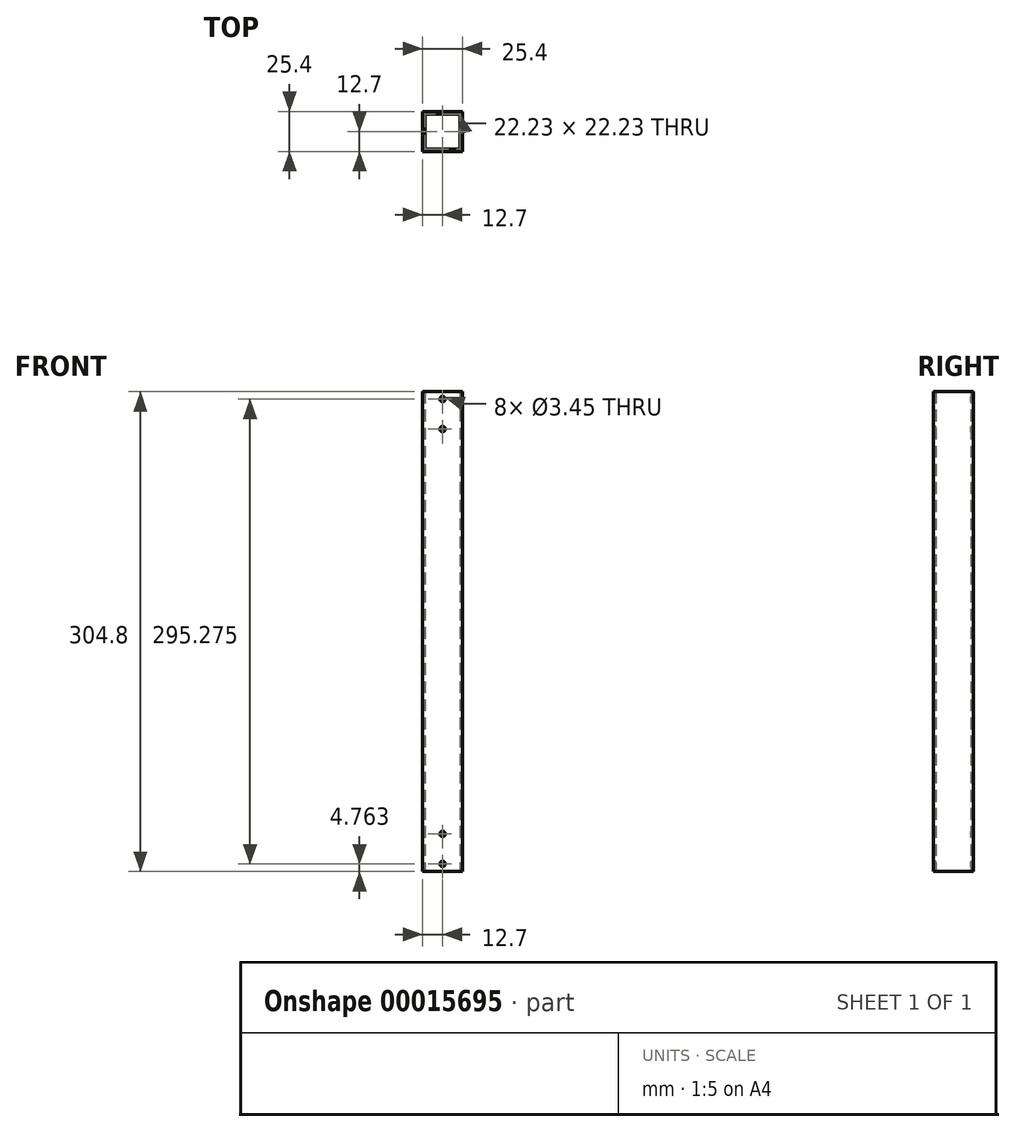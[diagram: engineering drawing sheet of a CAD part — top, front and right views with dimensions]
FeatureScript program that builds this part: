
annotation { "Feature Type Name" : "Feature", "Feature Type Description" : "" }
export const myFeature = defineFeature(function(context is Context, id is Id, definition is map)
    precondition{}
    {
        {
            var Q0;
            Q0=qCreatedBy(makeId("Top.planeOp"),FACE);
            var sketch = newSketch(context, id + "F0", { "sketchPlane" : qUnion([Q0])});
            skLineSegment(sketch, "E0.rect.bottom", {"start": v(12.7, -12.7) * mm, "end": v(-12.7, -12.7) * mm});
            skLineSegment(sketch, "E0.rect.top", {"start": v(12.7, 12.7) * mm, "end": v(-12.7, 12.7) * mm});
            skLineSegment(sketch, "E0.rect.left", {"start": v(12.7, -12.7) * mm, "end": v(12.7, 12.7) * mm});
            skLineSegment(sketch, "E0.rect.right", {"start": v(-12.7, -12.7) * mm, "end": v(-12.7, 12.7) * mm});
            skPoint(sketch, "E0.rect.middle", {"position": v(0, 0) * mm});
            skLineSegment(sketch, "E1.rect.bottom", {"start": v(11.11, -11.11) * mm, "end": v(-11.11, -11.11) * mm});
            skLineSegment(sketch, "E1.rect.top", {"start": v(11.11, 11.11) * mm, "end": v(-11.11, 11.11) * mm});
            skLineSegment(sketch, "E1.rect.left", {"start": v(11.11, -11.11) * mm, "end": v(11.11, 11.11) * mm});
            skLineSegment(sketch, "E1.rect.right", {"start": v(-11.11, -11.11) * mm, "end": v(-11.11, 11.11) * mm});
            skLineSegment(sketch, "E2", {"start": v(0, -11.11) * mm, "end": v(0, -12.7) * mm, "construction": true});
            skSolve(sketch);
        }
        {
            var Q0;
            Q0=qSketchRegion(id+"F0",true);
            extrude(context, id + "F1", {"entities" : qUnion([Q0]), "depth" : 304.8 * mm});
        }
        {
            var Q0;
            Q0=makeQuery(id+"F1.opExtrude","SWEPT_FACE",FACE,{"disambiguationData":[OSD([sQuery(id+"F0.wireOp",EDGE,"E0.rect.bottom")])]});
            var sketch = newSketch(context, id + "F2", { "sketchPlane" : qUnion([Q0])});
            skLineSegment(sketch, "E3", {"start": v(0, 0) * mm, "end": v(0, 4.76) * mm, "construction": true});
            skLineSegment(sketch, "E4", {"start": v(0, 4.76) * mm, "end": v(0, 23.81) * mm, "construction": true});
            skCircle(sketch, "E5", {"center": v(0, 23.81) * mm, "radius": 1.73 * mm});
            skCircle(sketch, "E6", {"center": v(0, 4.76) * mm, "radius": 1.73 * mm});
            skLineSegment(sketch, "E7", {"start": v(0, 304.8) * mm, "end": v(0, 300.04) * mm, "construction": true});
            skLineSegment(sketch, "E8", {"start": v(0, 300.04) * mm, "end": v(0, 280.99) * mm, "construction": true});
            skCircle(sketch, "E9", {"center": v(0, 300.04) * mm, "radius": 1.73 * mm});
            skCircle(sketch, "E10", {"center": v(0, 280.99) * mm, "radius": 1.73 * mm});
            skSolve(sketch);
        }
        {
            var Q0;
            Q0=qSketchRegion(id+"F2",true);
            var Q1;
            Q1=makeQuery(id+"F1.opExtrude","SWEPT_FACE",FACE,{"disambiguationData":[OSD([sQuery(id+"F0.wireOp",EDGE,"E0.rect.top")])]});
            extrude(context, id + "F3", {"entities" : qUnion([Q0]), "operationType" : NewBodyOperationType.REMOVE, "endBound" : BoundingType.UP_TO_SURFACE, "oppositeDirection" : true, "endBoundEntityFace" : qUnion([Q1]), "depth" : 25.4 * mm});
        }
    });
